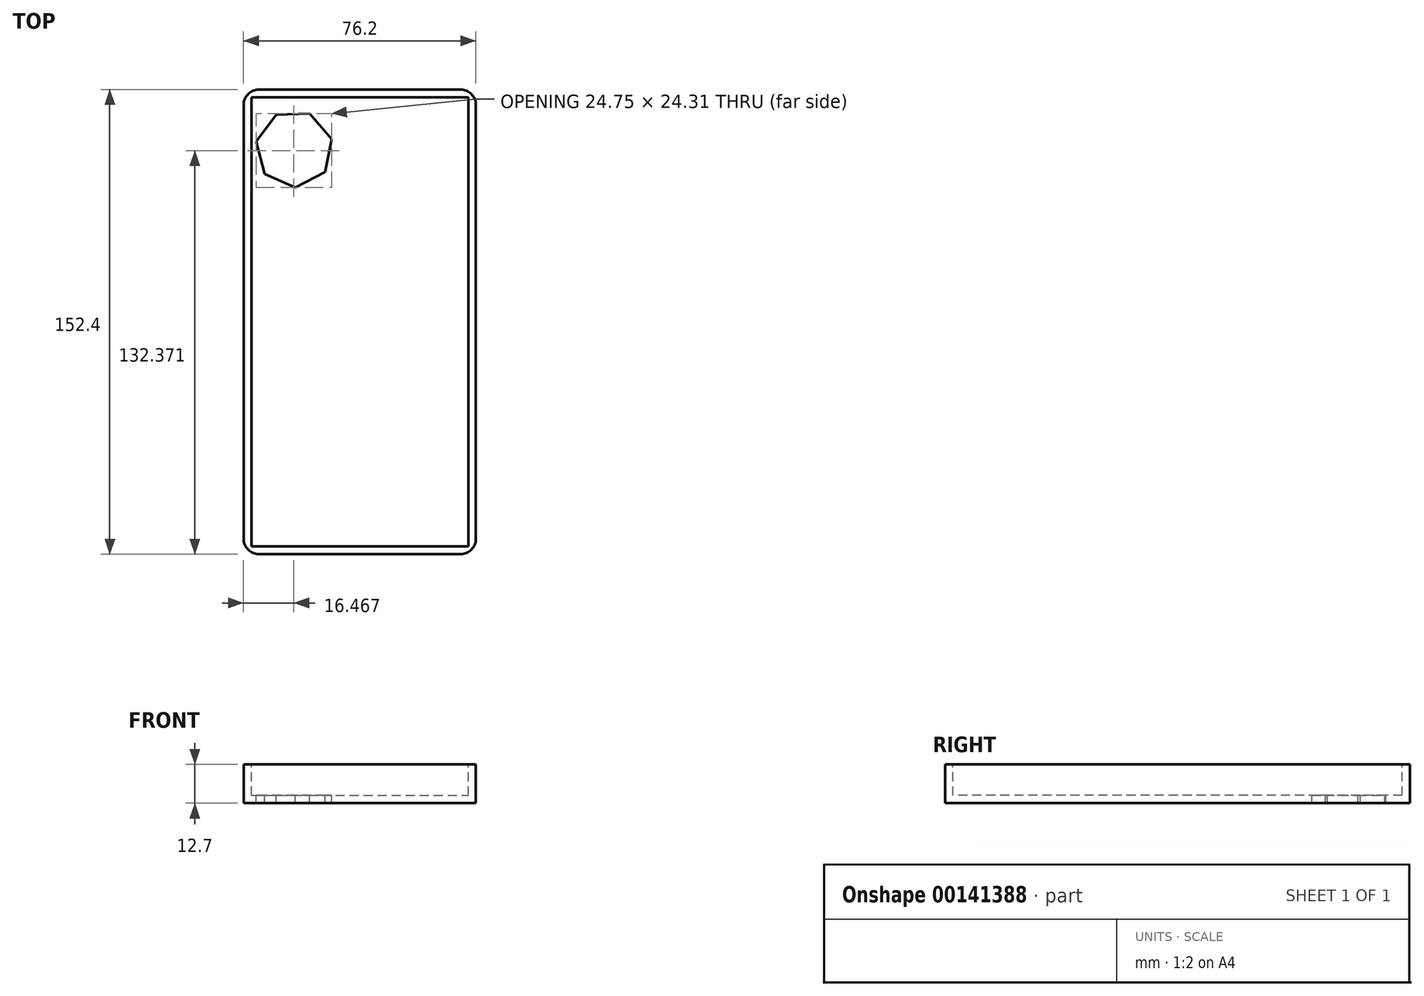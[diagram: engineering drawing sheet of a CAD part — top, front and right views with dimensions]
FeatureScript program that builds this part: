
annotation { "Feature Type Name" : "Feature", "Feature Type Description" : "" }
export const myFeature = defineFeature(function(context is Context, id is Id, definition is map)
    precondition{}
    {
        {
            var Q0;
            Q0=qCreatedBy(makeId("Top.planeOp"),FACE);
            var sketch = newSketch(context, id + "F0", { "sketchPlane" : qUnion([Q0])});
            skLineSegment(sketch, "E0.bottom", {"start": v(-42.26, 76) * mm, "end": v(33.94, 76) * mm});
            skLineSegment(sketch, "E0.top", {"start": v(-42.26, -76.4) * mm, "end": v(33.94, -76.4) * mm});
            skLineSegment(sketch, "E0.left", {"start": v(-42.26, 76) * mm, "end": v(-42.26, -76.4) * mm});
            skLineSegment(sketch, "E0.right", {"start": v(33.94, 76) * mm, "end": v(33.94, -76.4) * mm});
            skSolve(sketch);
        }
        {
            var Q0;
            Q0=makeQuery(id+"F0.imprint","IMPRINT",FACE,{"disambiguationData":[TD([[makeQuery(id+"F0.imprint","IMPRINT",EDGE,{"derivedFrom":sQuery(id+"F0.wireOp",EDGE,"E0.bottom")}),-1.0]])]});
            extrude(context, id + "F1", {"entities" : qUnion([Q0]), "oppositeDirection" : true, "depth" : 12.7 * mm});
        }
        {
            var Q0;
            Q0=makeQuery(id+"F1.opExtrude","CAP_FACE",FACE,{"disambiguationData":[OSD([sQuery(id+"F0.wireOp",EDGE,"E0.bottom"),sQuery(id+"F0.wireOp",EDGE,"E0.top"),sQuery(id+"F0.wireOp",EDGE,"E0.left"),sQuery(id+"F0.wireOp",EDGE,"E0.right")])],"isStart":true});
            shell(context, id + "F2", {"entities" : qUnion([Q0]), "thickness" : 2.54 * mm});
        }
        {
            var Q0;
            Q0=makeQuery(id+"F2.opShell","OFFSET_FACE",FACE,{"disambiguationData":[OSD([sQuery(id+"F0.wireOp",EDGE,"E0.bottom"),sQuery(id+"F0.wireOp",EDGE,"E0.top"),sQuery(id+"F0.wireOp",EDGE,"E0.left"),sQuery(id+"F0.wireOp",EDGE,"E0.right")])]});
            var sketch = newSketch(context, id + "F3", { "sketchPlane" : qUnion([Q0])});
            skCircle(sketch, "E1.cCircle", {"center": v(-25.7, 56.5) * mm, "radius": 12.7 * mm, "construction": true});
            skLineSegment(sketch, "E1.0", {"start": v(-25.28, 43.8) * mm, "end": v(-35.37, 48.26) * mm});
            skLineSegment(sketch, "E1.1", {"start": v(-35.37, 48.26) * mm, "end": v(-38.17, 58.92) * mm});
            skLineSegment(sketch, "E1.2", {"start": v(-38.17, 58.92) * mm, "end": v(-31.58, 67.76) * mm});
            skLineSegment(sketch, "E1.3", {"start": v(-31.58, 67.76) * mm, "end": v(-20.57, 68.12) * mm});
            skLineSegment(sketch, "E1.4", {"start": v(-20.57, 68.12) * mm, "end": v(-13.42, 59.73) * mm});
            skLineSegment(sketch, "E1.5", {"start": v(-13.42, 59.73) * mm, "end": v(-15.52, 48.91) * mm});
            skLineSegment(sketch, "E1.6", {"start": v(-15.52, 48.91) * mm, "end": v(-25.28, 43.8) * mm});
            skSolve(sketch);
        }
        {
            var Q0;
            Q0=makeQuery(id+"F3.imprint","IMPRINT",FACE,{"disambiguationData":[TD([[makeQuery(id+"F3.imprint","IMPRINT",EDGE,{"derivedFrom":sQuery(id+"F3.wireOp",EDGE,"E1.0")}),-1.0]])]});
            extrude(context, id + "F4", {"entities" : qUnion([Q0]), "operationType" : NewBodyOperationType.REMOVE, "oppositeDirection" : true, "depth" : 58.26 * mm});
        }
        {
            var Q0;
            Q0=makeQuery(id+"F1.opExtrude","SWEPT_EDGE",EDGE,{"disambiguationData":[OSD([sQuery(id+"F0.wireOp",EDGE,"E0.top"),sQuery(id+"F0.wireOp",EDGE,"E0.right")])]});
            var Q1;
            Q1=makeQuery(id+"F1.opExtrude","SWEPT_EDGE",EDGE,{"disambiguationData":[OSD([sQuery(id+"F0.wireOp",EDGE,"E0.top"),sQuery(id+"F0.wireOp",EDGE,"E0.left")])]});
            var Q2;
            Q2=makeQuery(id+"F1.opExtrude","SWEPT_EDGE",EDGE,{"disambiguationData":[OSD([sQuery(id+"F0.wireOp",EDGE,"E0.bottom"),sQuery(id+"F0.wireOp",EDGE,"E0.right")])]});
            var Q3;
            Q3=makeQuery(id+"F1.opExtrude","SWEPT_EDGE",EDGE,{"disambiguationData":[OSD([sQuery(id+"F0.wireOp",EDGE,"E0.bottom"),sQuery(id+"F0.wireOp",EDGE,"E0.left")])]});
            fillet(context, id + "F5", {"entities" : qUnion([Q0, Q1, Q2, Q3]), "radius" : 5.08 * mm, "tangentPropagation" : true, "allowEdgeOverflow" : false});
        }
    });
